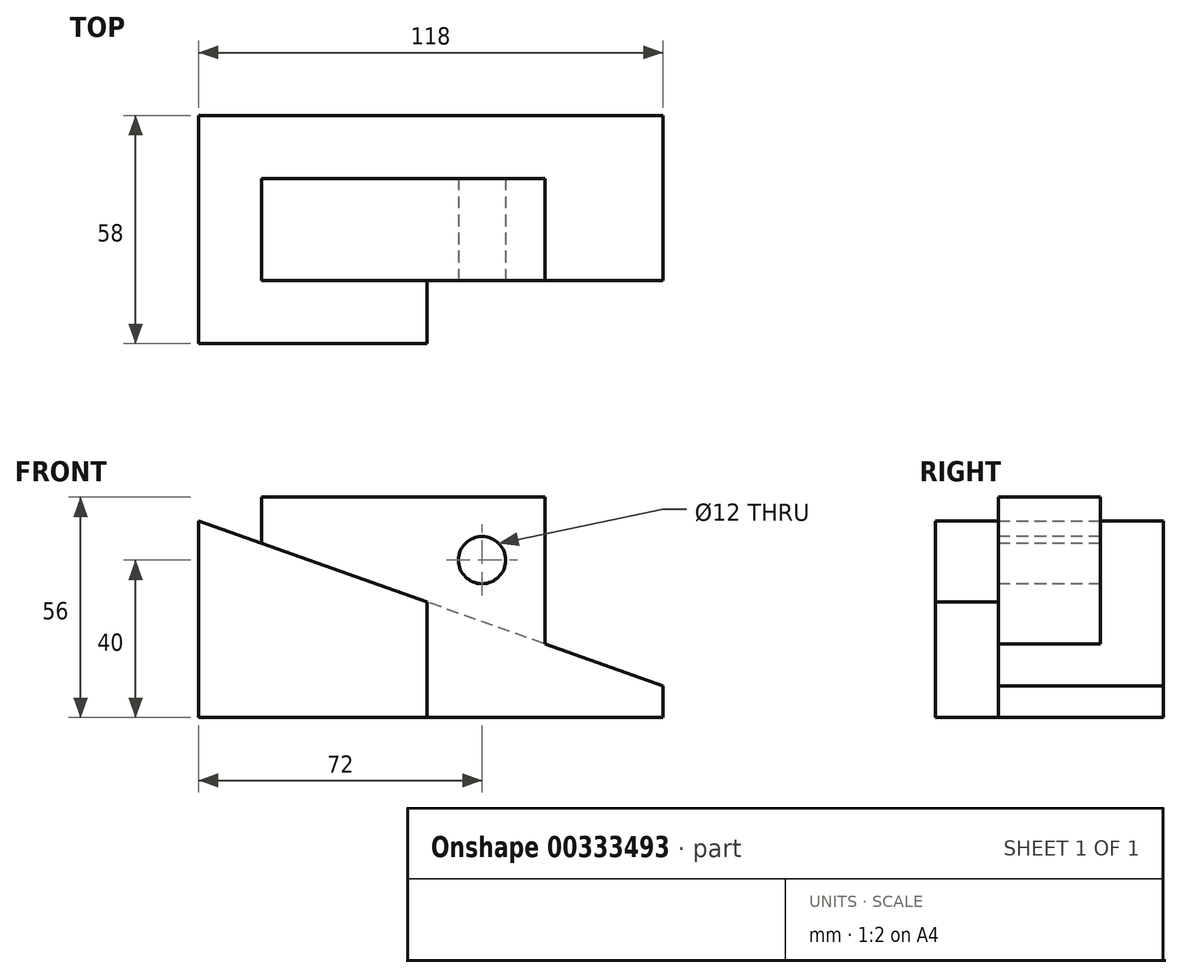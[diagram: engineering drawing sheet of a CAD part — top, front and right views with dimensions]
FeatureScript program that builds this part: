
annotation { "Feature Type Name" : "Feature", "Feature Type Description" : "" }
export const myFeature = defineFeature(function(context is Context, id is Id, definition is map)
    precondition{}
    {
        {
            var Q0;
            Q0=qCreatedBy(makeId("Front.planeOp"),FACE);
            var sketch = newSketch(context, id + "F0", { "sketchPlane" : qUnion([Q0])});
            skLineSegment(sketch, "E0", {"start": v(0, 0) * mm, "end": v(118, 0) * mm});
            skLineSegment(sketch, "E1", {"start": v(0, 50) * mm, "end": v(0, 0) * mm});
            skLineSegment(sketch, "E2", {"start": v(118, 0) * mm, "end": v(118, 8) * mm});
            skLineSegment(sketch, "E3", {"start": v(118, 8) * mm, "end": v(0, 50) * mm});
            skSolve(sketch);
        }
        {
            var Q0;
            Q0 = qSketchRegion(id + "F0", true);
            extrude(context, id + "F1", {"entities" : qUnion([Q0]), "depth" : 58 * mm});
        }
        {
            var Q0;
            Q0=qCreatedBy(makeId("Top.planeOp"),FACE);
            var sketch = newSketch(context, id + "F2", { "sketchPlane" : qUnion([Q0])});
            skLineSegment(sketch, "E4.0.2", {"start": v(58, -58) * mm, "end": v(118, -58) * mm});
            skLineSegment(sketch, "E4.0.3", {"start": v(118, -58) * mm, "end": v(118, -42) * mm});
            skLineSegment(sketch, "E5.bottom", {"start": v(118, -58) * mm, "end": v(58, -58) * mm});
            skLineSegment(sketch, "E5.top", {"start": v(118, -42) * mm, "end": v(58, -42) * mm});
            skLineSegment(sketch, "E5.right", {"start": v(58, -58) * mm, "end": v(58, -42) * mm});
            skPoint(sketch, "E4.0.1.end.orphan", {"position": v(0, -58) * mm});
            skPoint(sketch, "E4.0.0.end.orphan", {"position": v(0, 0) * mm});
            skPoint(sketch, "E6.orphan", {"position": v(118, 0) * mm});
            skSolve(sketch);
        }
        {
            var Q0;
            Q0 = qSketchRegion(id + "F2", true);
            extrude(context, id + "F3", {"entities" : qUnion([Q0]), "operationType" : NewBodyOperationType.REMOVE, "endBound" : BoundingType.THROUGH_ALL, "depth" : 25 * mm});
        }
        {
            var Q0;
            Q0=makeQuery(id+"F1.opExtrude","SWEPT_FACE",FACE,{"disambiguationData":[OSD([sQuery(id+"F0.wireOp",EDGE,"E0")])]});
            var sketch = newSketch(context, id + "F4", { "sketchPlane" : qUnion([Q0])});
            skLineSegment(sketch, "E7.bottom", {"start": v(88, 42) * mm, "end": v(16, 42) * mm});
            skLineSegment(sketch, "E7.top", {"start": v(88, 16) * mm, "end": v(16, 16) * mm});
            skLineSegment(sketch, "E7.left", {"start": v(88, 42) * mm, "end": v(88, 16) * mm});
            skLineSegment(sketch, "E7.right", {"start": v(16, 42) * mm, "end": v(16, 16) * mm});
            skSolve(sketch);
        }
        {
            var Q0;
            Q0 = qSketchRegion(id + "F4", true);
            extrude(context, id + "F5", {"entities" : qUnion([Q0]), "operationType" : NewBodyOperationType.ADD, "oppositeDirection" : true, "depth" : 56 * mm});
        }
        {
            var Q0;
            Q0=makeQuery(id+"F5.boolean.opBoolean","MERGE",FACE,{"derivedFrom":[makeQuery(id+"F3.boolean.opBoolean","COPY",FACE,{"derivedFrom":makeQuery(id+"F3.opExtrude","SWEPT_FACE",FACE,{"disambiguationData":[OSD([sQuery(id+"F2.wireOp",EDGE,"E5.top")])]})}),makeQuery(id+"F5.opExtrude","SWEPT_FACE",FACE,{"disambiguationData":[OSD([sQuery(id+"F4.wireOp",EDGE,"E7.bottom")])]})]});
            var sketch = newSketch(context, id + "F6", { "sketchPlane" : qUnion([Q0])});
            skCircle(sketch, "E8", {"center": v(72, 40) * mm, "radius": 6 * mm});
            skSolve(sketch);
        }
        {
            var Q0;
            Q0 = qSketchRegion(id + "F6", true);
            extrude(context, id + "F7", {"entities" : qUnion([Q0]), "operationType" : NewBodyOperationType.REMOVE, "endBound" : BoundingType.THROUGH_ALL, "oppositeDirection" : true, "depth" : 25 * mm});
        }
    });
